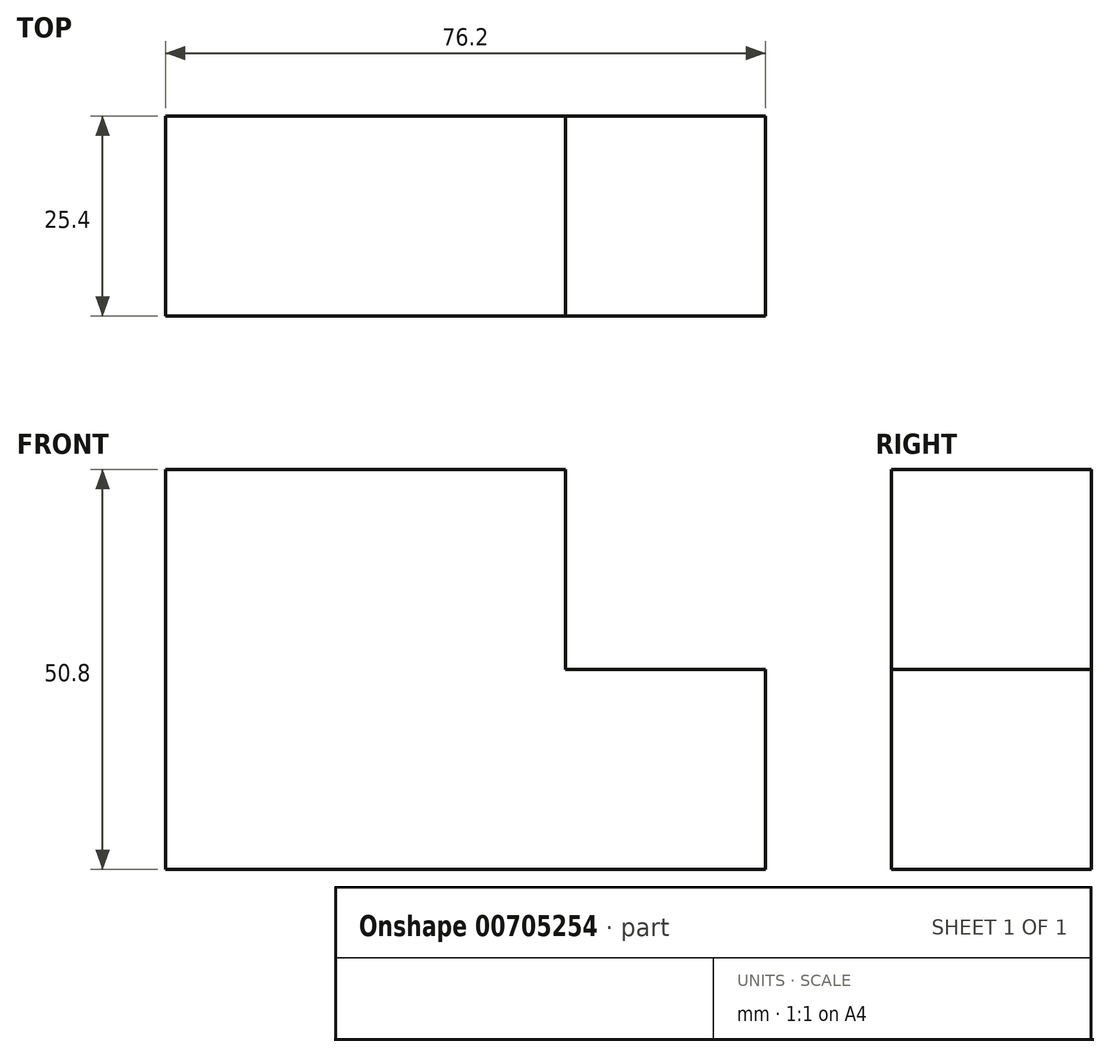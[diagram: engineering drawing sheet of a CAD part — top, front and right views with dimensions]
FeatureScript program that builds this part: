
annotation { "Feature Type Name" : "Feature", "Feature Type Description" : "" }
export const myFeature = defineFeature(function(context is Context, id is Id, definition is map)
    precondition{}
    {
        {
            var Q0;
            Q0=qCreatedBy(makeId("Front.planeOp"),FACE);
            var sketch = newSketch(context, id + "F0", { "sketchPlane" : qUnion([Q0])});
            skLineSegment(sketch, "E0.bottom", {"start": v(0, 25.4) * mm, "end": v(-25.4, 25.4) * mm});
            skLineSegment(sketch, "E0.top", {"start": v(0, 0) * mm, "end": v(-25.4, 0) * mm});
            skLineSegment(sketch, "E0.left", {"start": v(0, 25.4) * mm, "end": v(0, 0) * mm});
            skLineSegment(sketch, "E0.right", {"start": v(-25.4, 25.4) * mm, "end": v(-25.4, 0) * mm});
            skLineSegment(sketch, "E1.bottom", {"start": v(-25.4, 25.4) * mm, "end": v(-50.8, 25.4) * mm});
            skLineSegment(sketch, "E1.top", {"start": v(-25.4, 0) * mm, "end": v(-50.8, 0) * mm});
            skLineSegment(sketch, "E1.right", {"start": v(-50.8, 25.4) * mm, "end": v(-50.8, 0) * mm});
            skLineSegment(sketch, "E2.bottom", {"start": v(0, 25.4) * mm, "end": v(25.4, 25.4) * mm});
            skLineSegment(sketch, "E2.top", {"start": v(0, 0) * mm, "end": v(25.4, 0) * mm});
            skLineSegment(sketch, "E2.right", {"start": v(25.4, 25.4) * mm, "end": v(25.4, 0) * mm});
            skLineSegment(sketch, "E3.top", {"start": v(0, 50.8) * mm, "end": v(-25.4, 50.8) * mm});
            skLineSegment(sketch, "E3.left", {"start": v(0, 25.4) * mm, "end": v(0, 50.8) * mm});
            skLineSegment(sketch, "E3.right", {"start": v(-25.4, 25.4) * mm, "end": v(-25.4, 50.8) * mm});
            skLineSegment(sketch, "E4.bottom", {"start": v(-25.4, 50.8) * mm, "end": v(0, 50.8) * mm});
            skLineSegment(sketch, "E4.top", {"start": v(-25.4, 76.2) * mm, "end": v(0, 76.2) * mm});
            skLineSegment(sketch, "E4.left", {"start": v(-25.4, 50.8) * mm, "end": v(-25.4, 76.2) * mm});
            skLineSegment(sketch, "E4.right", {"start": v(0, 50.8) * mm, "end": v(0, 76.2) * mm});
            skLineSegment(sketch, "E5.bottom", {"start": v(-25.4, 50.8) * mm, "end": v(-50.8, 50.8) * mm});
            skLineSegment(sketch, "E5.left", {"start": v(-25.4, 50.8) * mm, "end": v(-25.4, 25.4) * mm});
            skLineSegment(sketch, "E5.right", {"start": v(-50.8, 50.8) * mm, "end": v(-50.8, 25.4) * mm});
            skSolve(sketch);
        }
        {
            var Q0;
            Q0=makeQuery(id+"F0.imprint","IMPRINT",FACE,{"disambiguationData":[TD([[makeQuery(id+"F0.imprint","IMPRINT",EDGE,{"derivedFrom":sQuery(id+"F0.wireOp",EDGE,"E5.bottom")}),1.0]])]});
            var Q1;
            Q1=makeQuery(id+"F0.imprint","IMPRINT",FACE,{"disambiguationData":[TD([[makeQuery(id+"F0.imprint","IMPRINT",EDGE,{"derivedFrom":sQuery(id+"F0.wireOp",EDGE,"E1.top")}),-1.0]])]});
            var Q2;
            Q2=makeQuery(id+"F0.imprint","IMPRINT",FACE,{"disambiguationData":[TD([[makeQuery(id+"F0.imprint","IMPRINT",EDGE,{"derivedFrom":sQuery(id+"F0.wireOp",EDGE,"E0.top")}),-1.0]])]});
            var Q3;
            Q3=makeQuery(id+"F0.imprint","IMPRINT",FACE,{"disambiguationData":[TD([[makeQuery(id+"F0.imprint","IMPRINT",EDGE,{"derivedFrom":sQuery(id+"F0.wireOp",EDGE,"E2.bottom")}),-1.0]])]});
            var Q4;
            Q4=makeQuery(id+"F0.imprint","IMPRINT",FACE,{"disambiguationData":[TD([[makeQuery(id+"F0.imprint","IMPRINT",EDGE,{"derivedFrom":sQuery(id+"F0.wireOp",EDGE,"E0.bottom")}),-1.0]])]});
            var Q5;
            Q5=makeQuery(id+"F0.imprint","IMPRINT",FACE,{"disambiguationData":[TD([[makeQuery(id+"F0.imprint","IMPRINT",EDGE,{"derivedFrom":sQuery(id+"F0.wireOp",EDGE,"E4.bottom")}),1.0]])]});
            extrude(context, id + "F1", {"entities" : qUnion([Q0, Q1, Q2, Q3, Q4, Q5]), "depth" : 25.4 * mm, "offsetDistance" : 25.4 * mm});
        }
    });
